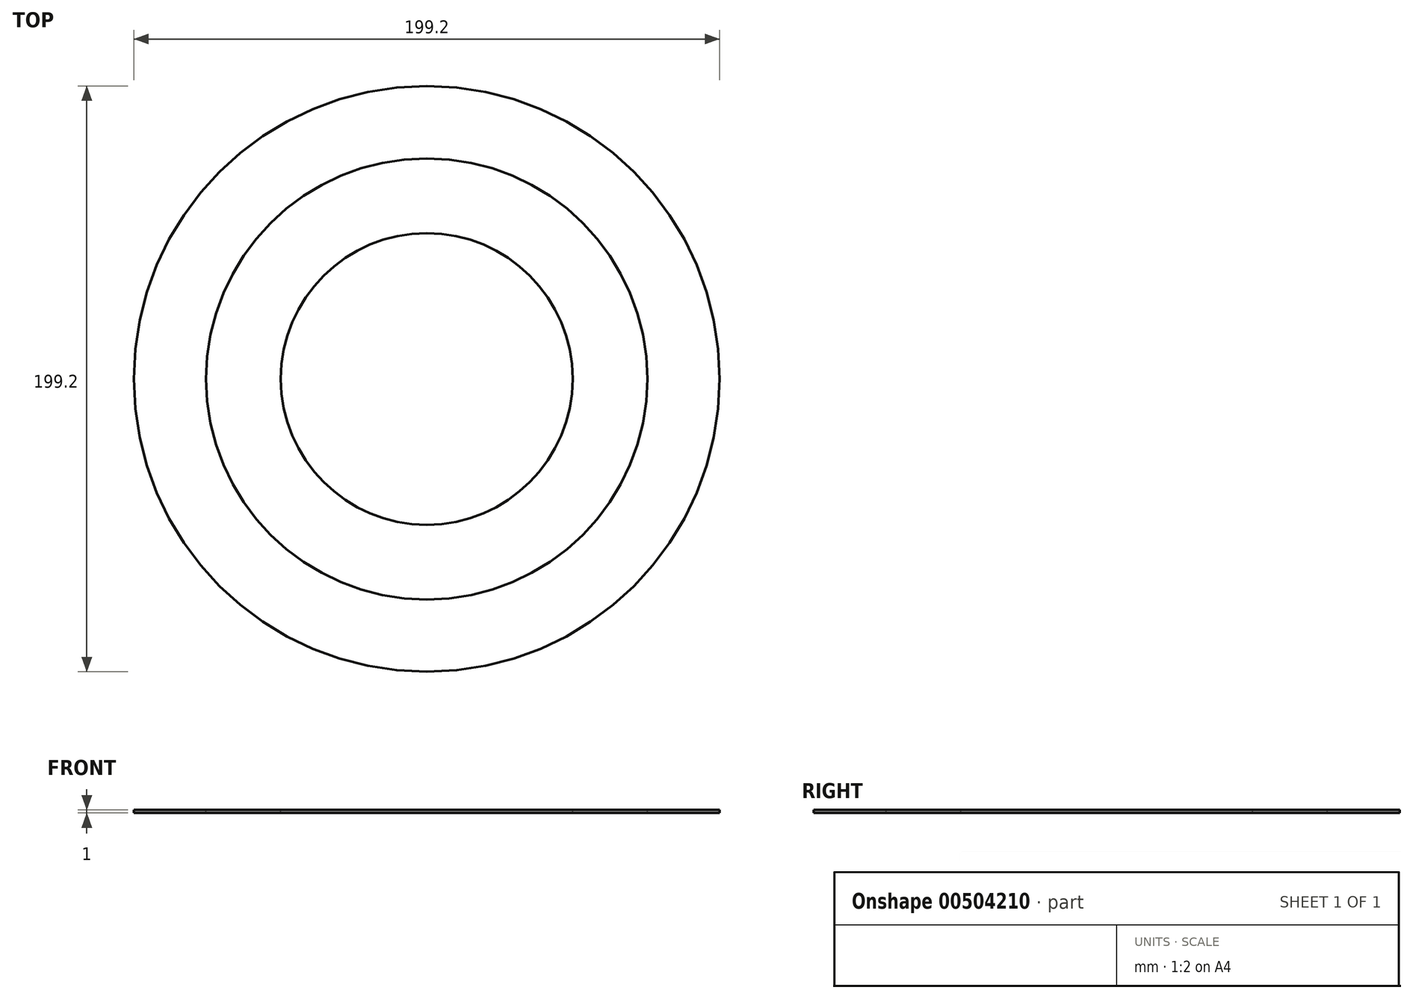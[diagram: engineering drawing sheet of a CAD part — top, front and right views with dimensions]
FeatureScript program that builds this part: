
annotation { "Feature Type Name" : "Feature", "Feature Type Description" : "" }
export const myFeature = defineFeature(function(context is Context, id is Id, definition is map)
    precondition{}
    {
        {
            var Q0;
            Q0=qCreatedBy(makeId("Top.planeOp"),FACE);
            var sketch = newSketch(context, id + "F0", { "sketchPlane" : qUnion([Q0])});
            skCircle(sketch, "E0", {"center": v(0, 0) * mm, "radius": 100 * mm});
            skCircle(sketch, "E1", {"center": v(0, 0) * mm, "radius": 99.6 * mm});
            skCircle(sketch, "E2", {"center": v(0, 0) * mm, "radius": 75 * mm});
            skCircle(sketch, "E3", {"center": v(0, 0) * mm, "radius": 74.6 * mm});
            skCircle(sketch, "E4", {"center": v(0, 0) * mm, "radius": 50 * mm});
            skCircle(sketch, "E5", {"center": v(0, 0) * mm, "radius": 49.6 * mm});
            skSolve(sketch);
        }
        {
            var Q0;
            Q0=makeQuery(id+"F0.imprint","IMPRINT",FACE,{"disambiguationData":[TD([[makeQuery(id+"F0.imprint","IMPRINT",EDGE,{"derivedFrom":sQuery(id+"F0.wireOp",EDGE,"E1")}),1.0]])]});
            var Q1;
            Q1=makeQuery(id+"F0.imprint","IMPRINT",FACE,{"disambiguationData":[TD([[makeQuery(id+"F0.imprint","IMPRINT",EDGE,{"derivedFrom":sQuery(id+"F0.wireOp",EDGE,"E3")}),1.0]])]});
            var Q2;
            Q2=makeQuery(id+"F0.imprint","IMPRINT",FACE,{"disambiguationData":[TD([[makeQuery(id+"F0.imprint","IMPRINT",EDGE,{"derivedFrom":sQuery(id+"F0.wireOp",EDGE,"E5")}),1.0]])]});
            var Q3;
            Q3=sQuery(id+"F0.wireOp",EDGE,"E1");
            var Q4;
            Q4=sQuery(id+"F0.wireOp",EDGE,"E2");
            var Q5;
            Q5=sQuery(id+"F0.wireOp",EDGE,"E5");
            extrude(context, id + "F1", {"entities" : qUnion([Q0, Q1, Q2]), "bodyType" : ToolBodyType.SURFACE, "surfaceEntities" : qUnion([Q3, Q4, Q5]), "depth" : 1 * mm});
        }
    });
